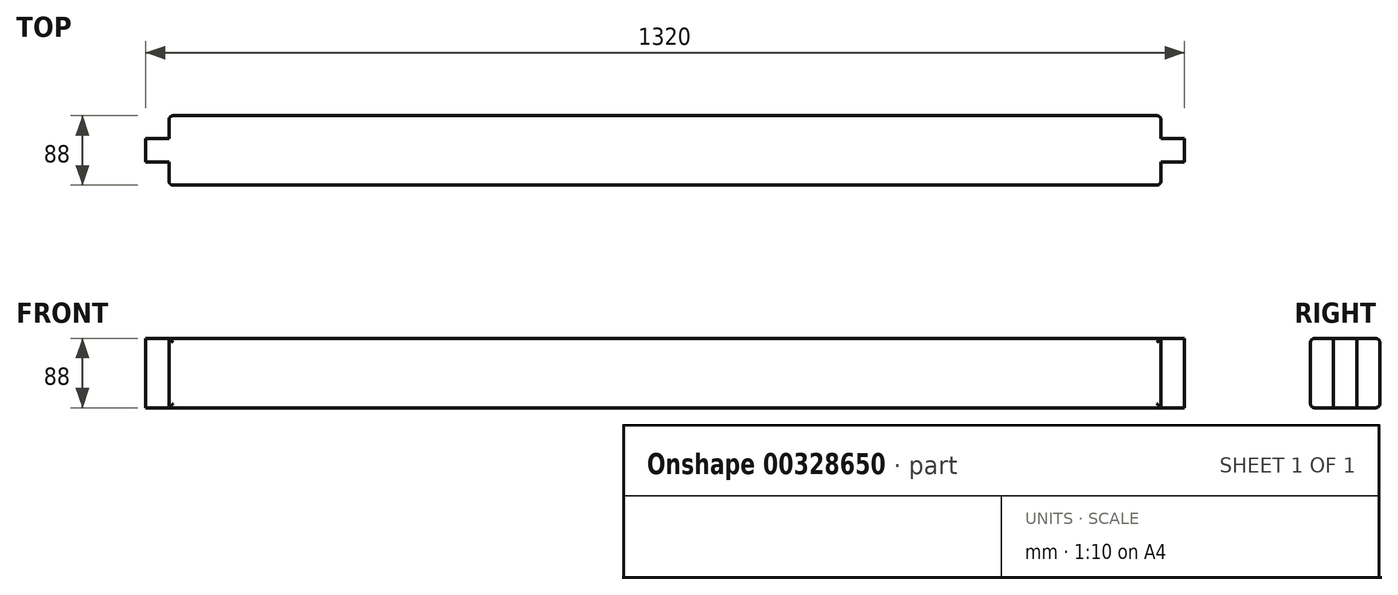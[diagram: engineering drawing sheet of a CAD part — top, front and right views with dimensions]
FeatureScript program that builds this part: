
annotation { "Feature Type Name" : "Feature", "Feature Type Description" : "" }
export const myFeature = defineFeature(function(context is Context, id is Id, definition is map)
    precondition{}
    {
        {
            var Q0;
            Q0=qCreatedBy(makeId("Top.planeOp"),FACE);
            var sketch = newSketch(context, id + "F0", { "sketchPlane" : qUnion([Q0])});
            skLineSegment(sketch, "E0.bottom", {"start": v(-630, -44) * mm, "end": v(630, -44) * mm});
            skLineSegment(sketch, "E0.top", {"start": v(-630, 44) * mm, "end": v(630, 44) * mm});
            skLineSegment(sketch, "E0.left", {"start": v(-660, -15) * mm, "end": v(-660, 15) * mm});
            skLineSegment(sketch, "E0.right", {"start": v(660, -15) * mm, "end": v(660, 15) * mm});
            skPoint(sketch, "E0.middle", {"position": v(0, 0) * mm});
            skLineSegment(sketch, "E1", {"start": v(-660, 15) * mm, "end": v(-630, 15) * mm});
            skLineSegment(sketch, "E2", {"start": v(-630, 15) * mm, "end": v(-630, 44) * mm});
            skLineSegment(sketch, "E3", {"start": v(-660, -15) * mm, "end": v(-630, -15) * mm});
            skLineSegment(sketch, "E4", {"start": v(-630, -15) * mm, "end": v(-630, -44) * mm});
            skPoint(sketch, "E5.orphan", {"position": v(-660, 44) * mm});
            skPoint(sketch, "E6.orphan", {"position": v(-660, -44) * mm});
            skLineSegment(sketch, "E7", {"start": v(660, 15) * mm, "end": v(630, 15) * mm});
            skLineSegment(sketch, "E8", {"start": v(630, 15) * mm, "end": v(630, 44) * mm});
            skLineSegment(sketch, "E9", {"start": v(660, -15) * mm, "end": v(630, -15) * mm});
            skLineSegment(sketch, "E10", {"start": v(630, -15) * mm, "end": v(630, -44) * mm});
            skPoint(sketch, "E11.orphan", {"position": v(660, 44) * mm});
            skPoint(sketch, "E12.orphan", {"position": v(660, -44) * mm});
            skSolve(sketch);
        }
        {
            var Q0;
            Q0=qSketchRegion(id+"F0",true);
            extrude(context, id + "F1", {"entities" : qUnion([Q0]), "depth" : 88 * mm});
        }
        {
            var Q0;
            Q0=makeQuery(id+"F1.opExtrude","CAP_EDGE",EDGE,{"disambiguationData":[OSD([sQuery(id+"F0.wireOp",EDGE,"E0.bottom")])],"isStart":true});
            var Q1;
            Q1=makeQuery(id+"F1.opExtrude","CAP_EDGE",EDGE,{"disambiguationData":[OSD([sQuery(id+"F0.wireOp",EDGE,"E0.bottom")])],"isStart":false});
            var Q2;
            Q2=makeQuery(id+"F1.opExtrude","CAP_EDGE",EDGE,{"disambiguationData":[OSD([sQuery(id+"F0.wireOp",EDGE,"E0.top")])],"isStart":false});
            var Q3;
            Q3=makeQuery(id+"F1.opExtrude","SWEPT_EDGE",EDGE,{"disambiguationData":[OSD([sQuery(id+"F0.wireOp",EDGE,"E0.bottom"),sQuery(id+"F0.wireOp",EDGE,"E10")])]});
            var Q4;
            Q4=makeQuery(id+"F1.opExtrude","SWEPT_EDGE",EDGE,{"disambiguationData":[OSD([sQuery(id+"F0.wireOp",EDGE,"E0.top"),sQuery(id+"F0.wireOp",EDGE,"E8")])]});
            var Q5;
            Q5=makeQuery(id+"F1.opExtrude","CAP_EDGE",EDGE,{"disambiguationData":[OSD([sQuery(id+"F0.wireOp",EDGE,"E0.top")])],"isStart":true});
            var Q6;
            Q6=makeQuery(id+"F1.opExtrude","SWEPT_EDGE",EDGE,{"disambiguationData":[OSD([sQuery(id+"F0.wireOp",EDGE,"E0.top"),sQuery(id+"F0.wireOp",EDGE,"E2")])]});
            var Q7;
            Q7=makeQuery(id+"F1.opExtrude","SWEPT_EDGE",EDGE,{"disambiguationData":[OSD([sQuery(id+"F0.wireOp",EDGE,"E0.bottom"),sQuery(id+"F0.wireOp",EDGE,"E4")])]});
            fillet(context, id + "F2", {"entities" : qUnion([Q0, Q1, Q2, Q3, Q4, Q5, Q6, Q7]), "radius" : 5 * mm, "tangentPropagation" : true, "allowEdgeOverflow" : false});
        }
    });
